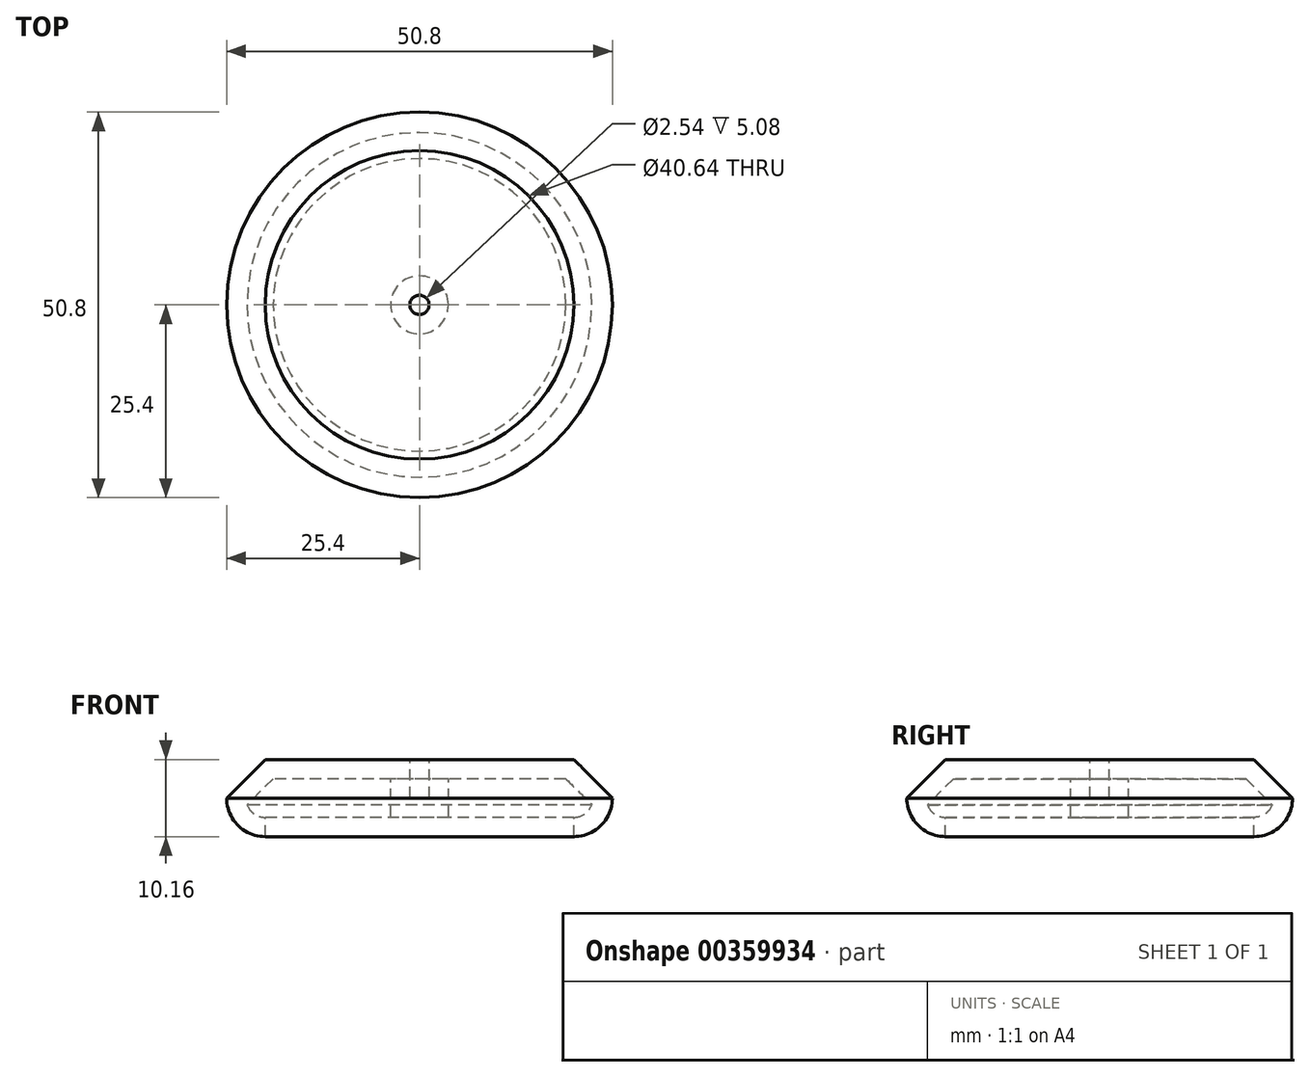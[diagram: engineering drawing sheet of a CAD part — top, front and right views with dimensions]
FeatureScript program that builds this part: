
annotation { "Feature Type Name" : "Feature", "Feature Type Description" : "" }
export const myFeature = defineFeature(function(context is Context, id is Id, definition is map)
    precondition{}
    {
        {
            var Q0;
            Q0=qCreatedBy(makeId("Top.planeOp"),FACE);
            var sketch = newSketch(context, id + "F0", { "sketchPlane" : qUnion([Q0])});
            skPoint(sketch, "E0", {"position": v(25.4, 0) * mm});
            skCircle(sketch, "E1", {"center": v(0, 0) * mm, "radius": 25.4 * mm});
            skSolve(sketch);
        }
        {
            var Q0;
            Q0 = qSketchRegion(id + "F0", true);
            extrude(context, id + "F1", {"entities" : qUnion([Q0]), "depth" : 10.16 * mm});
        }
        {
            var Q0;
            Q0=makeQuery(id+"F1.opExtrude","CAP_FACE",FACE,{"disambiguationData":[OSD([sQuery(id+"F0.wireOp",EDGE,"E1")])],"isStart":false});
            var sketch = newSketch(context, id + "F2", { "sketchPlane" : qUnion([Q0])});
            skPoint(sketch, "E2", {"position": v(1.27, 0) * mm});
            skCircle(sketch, "E3", {"center": v(0, 0) * mm, "radius": 1.27 * mm});
            skSolve(sketch);
        }
        {
            var Q0;
            Q0 = qSketchRegion(id + "F2", true);
            extrude(context, id + "F3", {"entities" : qUnion([Q0]), "operationType" : NewBodyOperationType.REMOVE, "oppositeDirection" : true, "depth" : 5.08 * mm});
        }
        {
            var Q0;
            Q0=makeQuery(id+"F1.opExtrude","CAP_EDGE",EDGE,{"disambiguationData":[OSD([sQuery(id+"F0.wireOp",EDGE,"E1")])],"isStart":false});
            chamfer(context, id + "F4", {"entities" : qUnion([Q0]), "width" : 5.08 * mm, "tangentPropagation" : true});
        }
        {
            var Q0;
            Q0=makeQuery(id+"F1.opExtrude","CAP_EDGE",EDGE,{"disambiguationData":[OSD([sQuery(id+"F0.wireOp",EDGE,"E1")])],"isStart":true});
            fillet(context, id + "F5", {"entities" : qUnion([Q0]), "radius" : 5.08 * mm, "tangentPropagation" : true, "allowEdgeOverflow" : false});
        }
        {
            var Q0;
            Q0=makeQuery(id+"F1.opExtrude","CAP_FACE",FACE,{"disambiguationData":[OSD([sQuery(id+"F0.wireOp",EDGE,"E1")])],"isStart":true});
            shell(context, id + "F6", {"entities" : qUnion([Q0]), "thickness" : 2.54 * mm});
        }
    });
